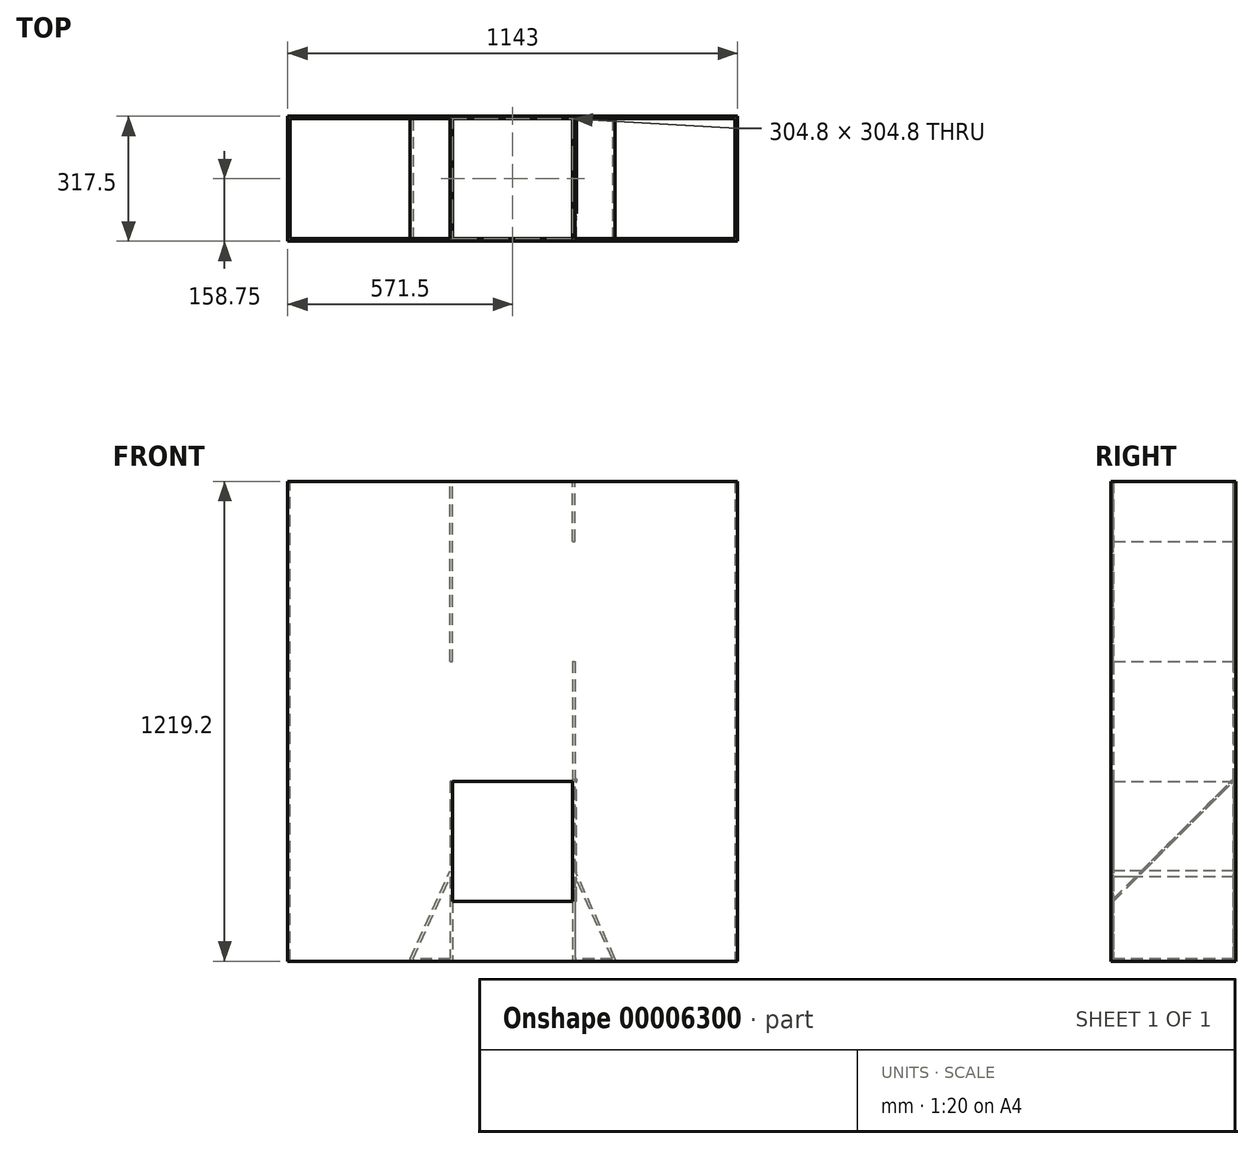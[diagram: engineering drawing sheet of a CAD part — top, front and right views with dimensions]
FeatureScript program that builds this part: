
annotation { "Feature Type Name" : "Feature", "Feature Type Description" : "" }
export const myFeature = defineFeature(function(context is Context, id is Id, definition is map)
    precondition{}
    {
        {
            var Q0;
            Q0=qCreatedBy(makeId("Front.planeOp"),FACE);
            var sketch = newSketch(context, id + "F0", { "sketchPlane" : qUnion([Q0])});
            skLineSegment(sketch, "E0", {"start": v(0, 0) * mm, "end": v(0, 1219.2) * mm});
            skLineSegment(sketch, "E1", {"start": v(0, 1219.2) * mm, "end": v(1143, 1219.2) * mm});
            skLineSegment(sketch, "E2", {"start": v(1143, 1219.2) * mm, "end": v(1143, 0) * mm});
            skLineSegment(sketch, "E3", {"start": v(1143, 0) * mm, "end": v(0, 0) * mm});
            skSolve(sketch);
        }
        {
            var Q0;
            Q0=makeQuery(id+"F0.imprint","IMPRINT",FACE,{"disambiguationData":[TD([[makeQuery(id+"F0.imprint","IMPRINT",EDGE,{"derivedFrom":sQuery(id+"F0.wireOp",EDGE,"E0")}),-1.0]])]});
            extrude(context, id + "F1", {"entities" : qUnion([Q0]), "depth" : 317.5 * mm});
        }
        {
            var Q0;
            Q0=sQuery(id+"F0.wireOp",EDGE,"E3");
            cPlane(context, id + "F2", {"entities" : qUnion([Q0]), "cplaneType" : CPlaneType.MID_PLANE, "offset" : 152.4 * mm, "width" : 152.4 * mm, "height" : 152.4 * mm});
        }
        {
            var Q0;
            Q0=makeQuery(id+"F1.opExtrude","SWEPT_FACE",FACE,{"disambiguationData":[OSD([sQuery(id+"F0.wireOp",EDGE,"E1")])]});
            shell(context, id + "F3", {"entities" : qUnion([Q0]), "thickness" : 6.35 * mm});
        }
        {
            var Q0;
            Q0=makeQuery(id+"F1.opExtrude","SWEPT_FACE",FACE,{"disambiguationData":[OSD([sQuery(id+"F0.wireOp",EDGE,"E3")])]});
            var sketch = newSketch(context, id + "F4", { "sketchPlane" : qUnion([Q0])});
            skLineSegment(sketch, "E4.0", {"start": v(0, 317.5) * mm, "end": v(0, 0) * mm});
            skLineSegment(sketch, "E4.1", {"start": v(1143, 317.5) * mm, "end": v(0, 317.5) * mm});
            skLineSegment(sketch, "E4.2", {"start": v(1143, 317.5) * mm, "end": v(1143, 0) * mm});
            skLineSegment(sketch, "E4.3", {"start": v(1143, 0) * mm, "end": v(0, 0) * mm});
            skLineSegment(sketch, "E5", {"start": v(0, 158.75) * mm, "end": v(1143, 158.75) * mm, "construction": true});
            skLineSegment(sketch, "E6", {"start": v(412.75, 311.15) * mm, "end": v(412.75, 6.35) * mm});
            skLineSegment(sketch, "E7", {"start": v(419.1, 311.15) * mm, "end": v(419.1, 6.35) * mm});
            skLineSegment(sketch, "E8.0", {"start": v(6.35, 311.15) * mm, "end": v(6.35, 6.35) * mm});
            skLineSegment(sketch, "E9", {"start": v(571.5, 311.15) * mm, "end": v(571.5, 0) * mm, "construction": true});
            skLineSegment(sketch, "E10.trimOffspring", {"start": v(571.5, 311.15) * mm, "end": v(6.35, 311.15) * mm});
            skLineSegment(sketch, "E11.trimOffspring", {"start": v(571.5, 6.35) * mm, "end": v(6.35, 6.35) * mm});
            skPoint(sketch, "E12.orphan", {"position": v(571.5, 317.5) * mm});
            skLineSegment(sketch, "E13.0.MirrorCS", {"start": v(723.9, 311.15) * mm, "end": v(723.9, 6.35) * mm});
            skLineSegment(sketch, "E14.0.MirrorCS", {"start": v(730.25, 311.15) * mm, "end": v(730.25, 6.35) * mm});
            skLineSegment(sketch, "E15.0.MirrorCS", {"start": v(1136.65, 311.15) * mm, "end": v(1136.65, 6.35) * mm});
            skLineSegment(sketch, "E16.0.MirrorCS", {"start": v(571.5, 311.15) * mm, "end": v(1136.65, 311.15) * mm});
            skLineSegment(sketch, "E17.0.MirrorCS", {"start": v(571.5, 6.35) * mm, "end": v(1136.65, 6.35) * mm});
            skLineSegment(sketch, "E18", {"start": v(311.15, 311.15) * mm, "end": v(311.15, 6.35) * mm});
            skLineSegment(sketch, "E19.0.MirrorCS", {"start": v(831.85, 311.15) * mm, "end": v(831.85, 6.35) * mm});
            skSolve(sketch);
        }
        {
            var Q0;
            {var subQ2=sQuery(id+"F4.wireOp",EDGE,"E8.0");Q0=makeQuery(id+"F4.imprint","IMPRINT",FACE,{"disambiguationData":[TD([[makeQuery(id+"F4.imprint","IMPRINT",EDGE,{"derivedFrom":subQ2}),1.0]])]});}
            var Q1;
            {var subQ7=sQuery(id+"F4.wireOp",EDGE,"E7");Q1=makeQuery(id+"F4.imprint","IMPRINT",FACE,{"disambiguationData":[TD([[makeQuery(id+"F4.imprint","IMPRINT",EDGE,{"derivedFrom":subQ7}),1.0]])]});}
            var Q2;
            {var subQ2=sQuery(id+"F4.wireOp",EDGE,"E15.0.MirrorCS");Q2=makeQuery(id+"F4.imprint","IMPRINT",FACE,{"disambiguationData":[TD([[makeQuery(id+"F4.imprint","IMPRINT",EDGE,{"derivedFrom":subQ2}),-1.0]])]});}
            var Q3;
            Q3=makeQuery(id+"F3.opShell","OFFSET_FACE",FACE,{"disambiguationData":[OSD([sQuery(id+"F0.wireOp",EDGE,"E3")])]});
            extrude(context, id + "F5", {"entities" : qUnion([Q0, Q1, Q2]), "operationType" : NewBodyOperationType.REMOVE, "endBound" : BoundingType.UP_TO_SURFACE, "oppositeDirection" : true, "endBoundEntityFace" : qUnion([Q3]), "depth" : 25.4 * mm});
        }
        {
            var Q0;
            {var subQ2=sQuery(id+"F4.wireOp",EDGE,"E13.0.MirrorCS");Q0=makeQuery(id+"F4.imprint","IMPRINT",FACE,{"disambiguationData":[TD([[makeQuery(id+"F4.imprint","IMPRINT",EDGE,{"derivedFrom":subQ2}),1.0]])]});}
            extrude(context, id + "F6", {"entities" : qUnion([Q0]), "operationType" : NewBodyOperationType.ADD, "oppositeDirection" : true, "depth" : 762 * mm});
        }
        {
            var Q0;
            {var subQ2=sQuery(id+"F4.wireOp",EDGE,"E6");Q0=makeQuery(id+"F4.imprint","IMPRINT",FACE,{"disambiguationData":[TD([[makeQuery(id+"F4.imprint","IMPRINT",EDGE,{"derivedFrom":subQ2}),1.0]])]});}
            extrude(context, id + "F7", {"entities" : qUnion([Q0]), "operationType" : NewBodyOperationType.ADD, "oppositeDirection" : true, "depth" : 457.2 * mm});
        }
        {
            var Q0;
            Q0=makeQuery(id+"F1.opExtrude","SWEPT_FACE",FACE,{"disambiguationData":[OSD([sQuery(id+"F0.wireOp",EDGE,"E1")])]});
            var sketch = newSketch(context, id + "F8", { "sketchPlane" : qUnion([Q0])});
            skLineSegment(sketch, "E20.0", {"start": v(723.9, -311.15) * mm, "end": v(723.9, -6.35) * mm});
            skLineSegment(sketch, "E21.0", {"start": v(730.25, -311.15) * mm, "end": v(730.25, -6.35) * mm});
            skLineSegment(sketch, "E22.0", {"start": v(6.35, -311.15) * mm, "end": v(1136.65, -311.15) * mm});
            skLineSegment(sketch, "E23.0", {"start": v(419.1, -311.15) * mm, "end": v(419.1, -6.35) * mm});
            skLineSegment(sketch, "E24.0", {"start": v(412.75, -311.15) * mm, "end": v(412.75, -6.35) * mm});
            skLineSegment(sketch, "E25.0", {"start": v(6.35, -6.35) * mm, "end": v(1136.65, -6.35) * mm});
            skSolve(sketch);
        }
        {
            var Q0;
            Q0=makeQuery(id+"F1.opExtrude","CAP_FACE",FACE,{"disambiguationData":[OSD([sQuery(id+"F0.wireOp",EDGE,"E0"),sQuery(id+"F0.wireOp",EDGE,"E1"),sQuery(id+"F0.wireOp",EDGE,"E2"),sQuery(id+"F0.wireOp",EDGE,"E3")])],"isStart":false});
            var sketch = newSketch(context, id + "F9", { "sketchPlane" : qUnion([Q0])});
            skLineSegment(sketch, "E26", {"start": v(571.5, 0) * mm, "end": v(571.5, 1219.2) * mm, "construction": true});
            skLineSegment(sketch, "E27.0", {"start": v(412.75, 1219.2) * mm, "end": v(412.75, 6.35) * mm});
            skLineSegment(sketch, "E28.0", {"start": v(412.75, 6.35) * mm, "end": v(311.15, 6.35) * mm});
            skLineSegment(sketch, "E29", {"start": v(311.15, 6.35) * mm, "end": v(412.75, 229.79) * mm});
            skLineSegment(sketch, "E30", {"start": v(318.13, 6.35) * mm, "end": v(412.75, 214.45) * mm});
            skLineSegment(sketch, "E31.0.MirrorCS", {"start": v(824.87, 6.35) * mm, "end": v(730.25, 214.45) * mm});
            skLineSegment(sketch, "E32.0.MirrorCS", {"start": v(831.85, 6.35) * mm, "end": v(730.25, 229.79) * mm});
            skLineSegment(sketch, "E33.0.MirrorCS", {"start": v(730.25, 6.35) * mm, "end": v(831.85, 6.35) * mm});
            skLineSegment(sketch, "E34.0", {"start": v(419.1, 1219.2) * mm, "end": v(419.1, 0) * mm});
            skLineSegment(sketch, "E35.0", {"start": v(0, 1219.2) * mm, "end": v(1143, 1219.2) * mm});
            skLineSegment(sketch, "E36.0.MirrorCS", {"start": v(730.25, 1219.2) * mm, "end": v(730.25, 6.35) * mm});
            skLineSegment(sketch, "E37.0.MirrorCS", {"start": v(723.9, 1219.2) * mm, "end": v(723.9, 0) * mm});
            skLineSegment(sketch, "E38", {"start": v(419.1, 152.4) * mm, "end": v(730.25, 152.4) * mm});
            skLineSegment(sketch, "E39", {"start": v(723.9, 457.2) * mm, "end": v(412.75, 457.2) * mm});
            skSolve(sketch);
        }
        {
            var Q0;
            {var subQ1=sQuery(id+"F9.wireOp",EDGE,"E29");Q0=makeQuery(id+"F9.imprint","IMPRINT",FACE,{"disambiguationData":[TD([[makeQuery(id+"F9.imprint","IMPRINT",EDGE,{"derivedFrom":subQ1}),-1.0]])]});}
            var Q1;
            {var subQ2=sQuery(id+"F9.wireOp",EDGE,"E31.0.MirrorCS");Q1=makeQuery(id+"F9.imprint","IMPRINT",FACE,{"disambiguationData":[TD([[makeQuery(id+"F9.imprint","IMPRINT",EDGE,{"derivedFrom":subQ2}),-1.0]])]});}
            var Q2;
            Q2=sQuery(id+"F9.wireOp",EDGE,"E29");
            var Q3;
            Q3=sQuery(id+"F9.wireOp",EDGE,"E30");
            var Q4;
            Q4=makeQuery(id+"F1.opExtrude","CAP_FACE",FACE,{"disambiguationData":[OSD([sQuery(id+"F0.wireOp",EDGE,"E0"),sQuery(id+"F0.wireOp",EDGE,"E1"),sQuery(id+"F0.wireOp",EDGE,"E2"),sQuery(id+"F0.wireOp",EDGE,"E3")])],"isStart":true});
            extrude(context, id + "F10", {"entities" : qUnion([Q0, Q1]), "operationType" : NewBodyOperationType.ADD, "surfaceEntities" : qUnion([Q2, Q3]), "endBound" : BoundingType.UP_TO_SURFACE, "oppositeDirection" : true, "endBoundEntityFace" : qUnion([Q4]), "depth" : 25.4 * mm});
        }
        {
            var Q0;
            {var subQ1=sQuery(id+"F9.wireOp",EDGE,"E34.0");var subQ5=sQuery(id+"F9.wireOp",EDGE,"E38");var subQ7=makeQuery(id+"F9.imprint","INTERSECT",VERTEX,{"derivedFrom":[subQ1,subQ5]});Q0=makeQuery(id+"F9.imprint","IMPRINT",FACE,{"disambiguationData":[TD([[makeQuery(id+"F9.imprint","IMPRINT",EDGE,{"disambiguationData":[TD([[subQ7,1.0]])],"derivedFrom":subQ1}),1.0]])]});}
            var Q1;
            {var subQ0=sQuery(id+"F0.wireOp",EDGE,"E0");var subQ1=sQuery(id+"F0.wireOp",EDGE,"E1");var subQ2=sQuery(id+"F0.wireOp",EDGE,"E2");var subQ3=sQuery(id+"F0.wireOp",EDGE,"E3");var subQ4=sQuery(id+"F4.wireOp",EDGE,"E10.trimOffspring");var subQ5=sQuery(id+"F4.wireOp",EDGE,"E16.0.MirrorCS");var subQ6=makeQuery(id+"F5.boolean.opBoolean","MERGE",FACE,{"derivedFrom":[makeQuery(id+"F3.opShell","OFFSET_FACE",FACE,{"disambiguationData":[OSD([subQ0,subQ1,subQ2,subQ3]),TDD([makeQuery(id+"F1.opExtrude","CAP_FACE",FACE,{"disambiguationData":[OSD([subQ0,subQ1,subQ2,subQ3])],"isStart":false})])]}),makeQuery(id+"F5.opExtrude","SWEPT_FACE",FACE,{"disambiguationData":[OSD([subQ4,subQ5])]}),makeQuery(id+"F5.opExtrude","SWEPT_FACE",FACE,{"disambiguationData":[OSD([subQ4])]}),makeQuery(id+"F5.opExtrude","SWEPT_FACE",FACE,{"disambiguationData":[OSD([subQ5])]})]});Q1=qUnion([makeQuery(id+"F10.boolean.opBoolean","SPLIT",FACE,{"disambiguationData":[TD([makeQuery(id+"F1.opExtrude","SWEPT_FACE",FACE,{"disambiguationData":[OSD([subQ1])]})])],"derivedFrom":subQ6}),makeQuery(id+"F10.boolean.opBoolean","SPLIT",FACE,{"disambiguationData":[TD([makeQuery(id+"F10.opExtrude","SWEPT_FACE",FACE,{"disambiguationData":[OSD([sQuery(id+"F9.wireOp",EDGE,"E30")])]})])],"derivedFrom":subQ6}),makeQuery(id+"F10.boolean.opBoolean","SPLIT",FACE,{"disambiguationData":[TD([makeQuery(id+"F10.opExtrude","SWEPT_FACE",FACE,{"disambiguationData":[OSD([sQuery(id+"F9.wireOp",EDGE,"E31.0.MirrorCS")])]})])],"derivedFrom":subQ6})]);}
            extrude(context, id + "F11", {"entities" : qUnion([Q0]), "operationType" : NewBodyOperationType.REMOVE, "endBound" : BoundingType.UP_TO_SURFACE, "oppositeDirection" : true, "endBoundEntityFace" : qUnion([Q1]), "depth" : 25.4 * mm});
        }
        {
            var Q0;
            {var subQ0=sQuery(id+"F4.wireOp",EDGE,"E14.0.MirrorCS");Q0=makeQuery(id+"F10.boolean.opBoolean","SPLIT",FACE,{"disambiguationData":[TD([makeQuery(id+"F10.opExtrude","SWEPT_FACE",FACE,{"disambiguationData":[OSD([sQuery(id+"F9.wireOp",EDGE,"E32.0.MirrorCS")])]})])],"derivedFrom":makeQuery(id+"F6.opExtrude","SWEPT_FACE",FACE,{"disambiguationData":[OSD([subQ0])]})});}
            var sketch = newSketch(context, id + "F12", { "sketchPlane" : qUnion([Q0])});
            skLineSegment(sketch, "E40.0", {"start": v(-311.15, 152.4) * mm, "end": v(-317.5, 152.4) * mm});
            skLineSegment(sketch, "E41", {"start": v(-311.15, 152.4) * mm, "end": v(-6.35, 457.2) * mm});
            skLineSegment(sketch, "E42.0", {"start": v(-6.35, 762) * mm, "end": v(-6.35, 229.79) * mm});
            skLineSegment(sketch, "E43", {"start": v(-317.5, 152.4) * mm, "end": v(-6.35, 463.55) * mm});
            skSolve(sketch);
        }
        {
            var Q0;
            {var subQ3=sQuery(id+"F12.wireOp",EDGE,"E41");var subQ6=sQuery(id+"F12.wireOp",EDGE,"E40.0");var subQ7=sQuery(id+"F12.wireOp",EDGE,"E42.0");var subQ9=makeQuery(id+"F12.imprint","INTERSECT",VERTEX,{"derivedFrom":[subQ3,subQ7]});Q0=qUnion([makeQuery(id+"F12.imprint","IMPRINT",FACE,{"disambiguationData":[TD([[makeQuery(id+"F12.imprint","IMPRINT",EDGE,{"derivedFrom":subQ6}),-1.0]])]}),makeQuery(id+"F12.imprint","IMPRINT",FACE,{"disambiguationData":[TD([[makeQuery(id+"F12.imprint","IMPRINT",EDGE,{"disambiguationData":[TD([[subQ9,1.0]])],"derivedFrom":subQ7}),-1.0]])]})]);}
            extrude(context, id + "F13", {"entities" : qUnion([Q0]), "operationType" : NewBodyOperationType.ADD, "depth" : 3.17 * mm});
        }
        {
            var Q0;
            {var subQ2=sQuery(id+"F8.wireOp",EDGE,"E23.0");Q0=makeQuery(id+"F8.imprint","IMPRINT",FACE,{"disambiguationData":[TD([[makeQuery(id+"F8.imprint","IMPRINT",EDGE,{"derivedFrom":subQ2}),1.0]])]});}
            extrude(context, id + "F14", {"entities" : qUnion([Q0]), "operationType" : NewBodyOperationType.ADD, "oppositeDirection" : true, "depth" : 457.2 * mm});
        }
        {
            var Q0;
            {var subQ2=sQuery(id+"F8.wireOp",EDGE,"E20.0");Q0=makeQuery(id+"F8.imprint","IMPRINT",FACE,{"disambiguationData":[TD([[makeQuery(id+"F8.imprint","IMPRINT",EDGE,{"derivedFrom":subQ2}),-1.0]])]});}
            extrude(context, id + "F15", {"entities" : qUnion([Q0]), "operationType" : NewBodyOperationType.ADD, "oppositeDirection" : true, "depth" : 152.4 * mm});
        }
    });
